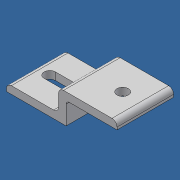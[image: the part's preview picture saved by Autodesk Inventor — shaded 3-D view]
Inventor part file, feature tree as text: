
AUTODESK INVENTOR PART (.ipt)
format: ipt  version: 2012 (Build 160160000, 160)  size: 112,640 bytes
history: native  units: mm (DEFAULTED — no unit token found)
features: sketch x3, extrude x2, fillet x2, hole x1
ambient origin geometry x8: Origin, YZ Plane, XZ Plane, XY Plane, X Axis, Y Axis, Z Axis, Center Point
bodies: Solid1 (feature_tree)
feature tree (8):
  extrude  "Extrusion1"  Depth=6.0mm
  hole  "Hole1"  [1 undecoded]
  extrude  "Extrusion2"  Depth=17.5mm
  fillet  "Fillet2"  Radius=45.0mm
  fillet  "Fillet3"  Radius=22.5044mm
  sketch  "Sketch1"  dims[d0=6.0mm d1=6.0mm]
  sketch  "Sketch3"  dims[d2=6.0mm d3=88.0mm]
  sketch  "Sketch4"  dims[d4=41.5mm d5=17.5mm d6=45.0mm d7=0.0mm d9=22.5044mm d10=22.5044mm d11=9.0mm d12=19.05mm d13=9.525mm d14=6.35mm d15=14.3117mm d16=25.4mm d17=20.594885mm d18=17.5mm d19=18.0mm d20=22.5044mm d21=9.0mm d22=9.0mm d23=45.0mm d24=0.0mm d25=2.5mm d26=4.0mm]
note: 1 required parameter value undecoded (feature->parameter linkage not recoverable at this tier; creation-order binding heuristic only, values carry confidence <= 0.55)
